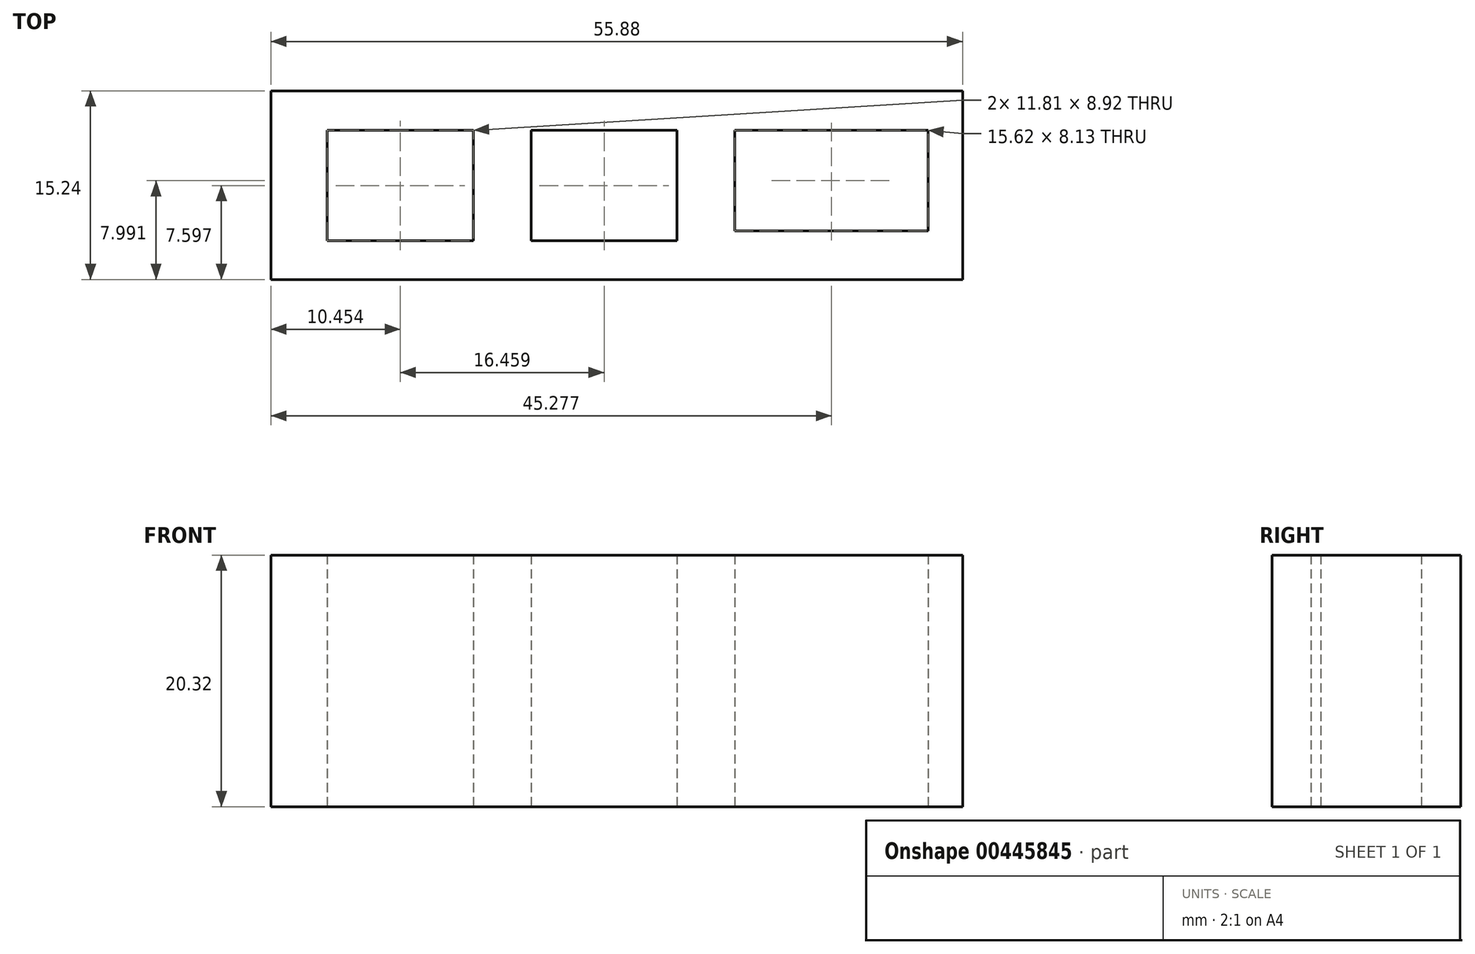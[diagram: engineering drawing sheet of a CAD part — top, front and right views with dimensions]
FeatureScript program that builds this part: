
annotation { "Feature Type Name" : "Feature", "Feature Type Description" : "" }
export const myFeature = defineFeature(function(context is Context, id is Id, definition is map)
    precondition{}
    {
        {
            var Q0;
            Q0=qCreatedBy(makeId("Top.planeOp"),FACE);
            var sketch = newSketch(context, id + "F0", { "sketchPlane" : qUnion([Q0])});
            skLineSegment(sketch, "E0.bottom", {"start": v(0, 0) * mm, "end": v(55.88, 0) * mm});
            skLineSegment(sketch, "E0.top", {"start": v(0, 15.24) * mm, "end": v(55.88, 15.24) * mm});
            skLineSegment(sketch, "E0.left", {"start": v(0, 0) * mm, "end": v(0, 15.24) * mm});
            skLineSegment(sketch, "E0.right", {"start": v(55.88, 0) * mm, "end": v(55.88, 15.24) * mm});
            skLineSegment(sketch, "E1.bottom", {"start": v(4.55, 12.06) * mm, "end": v(16.36, 12.06) * mm});
            skLineSegment(sketch, "E1.top", {"start": v(4.55, 3.14) * mm, "end": v(16.36, 3.14) * mm});
            skLineSegment(sketch, "E1.left", {"start": v(4.55, 12.06) * mm, "end": v(4.55, 3.14) * mm});
            skLineSegment(sketch, "E1.right", {"start": v(16.36, 12.06) * mm, "end": v(16.36, 3.14) * mm});
            skLineSegment(sketch, "E2.bottom", {"start": v(21, 12.06) * mm, "end": v(32.82, 12.06) * mm});
            skLineSegment(sketch, "E2.top", {"start": v(21, 3.14) * mm, "end": v(32.82, 3.14) * mm});
            skLineSegment(sketch, "E2.left", {"start": v(21, 12.06) * mm, "end": v(21, 3.14) * mm});
            skLineSegment(sketch, "E2.right", {"start": v(32.82, 12.06) * mm, "end": v(32.82, 3.14) * mm});
            skLineSegment(sketch, "E3.bottom", {"start": v(37.47, 12.06) * mm, "end": v(53.09, 12.06) * mm});
            skLineSegment(sketch, "E3.top", {"start": v(37.47, 3.93) * mm, "end": v(53.09, 3.93) * mm});
            skLineSegment(sketch, "E3.left", {"start": v(37.47, 12.06) * mm, "end": v(37.47, 3.93) * mm});
            skLineSegment(sketch, "E3.right", {"start": v(53.09, 12.06) * mm, "end": v(53.09, 3.93) * mm});
            skLineSegment(sketch, "E4", {"start": v(16.36, 12.06) * mm, "end": v(55.88, 12.06) * mm, "construction": true});
            skSolve(sketch);
        }
        {
            var Q0;
            Q0 = qSketchRegion(id + "F0", true);
            extrude(context, id + "F1", {"entities" : qUnion([Q0]), "depth" : 20.32 * mm});
        }
    });
